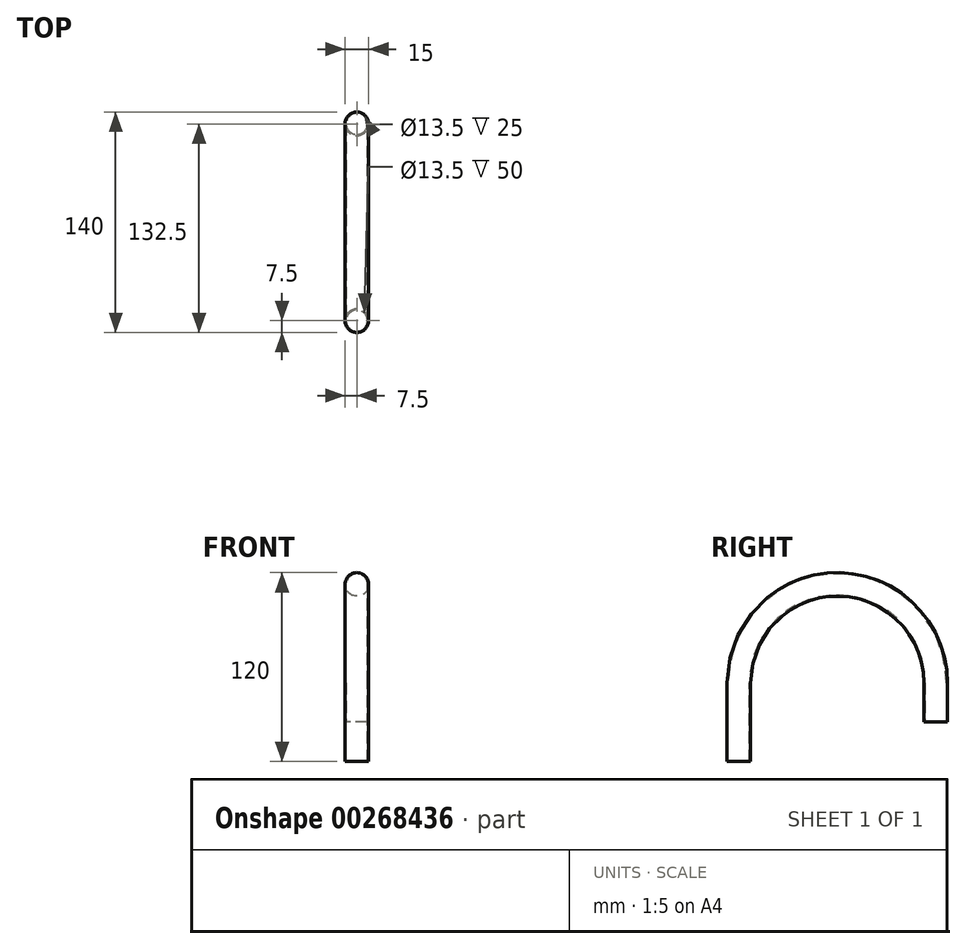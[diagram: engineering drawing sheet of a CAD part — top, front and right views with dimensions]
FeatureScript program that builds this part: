
annotation { "Feature Type Name" : "Feature", "Feature Type Description" : "" }
export const myFeature = defineFeature(function(context is Context, id is Id, definition is map)
    precondition{}
    {
        {
            var Q0;
            Q0=qCreatedBy(makeId("Top.planeOp"),FACE);
            var sketch = newSketch(context, id + "F0", { "sketchPlane" : qUnion([Q0])});
            skCircle(sketch, "E0", {"center": v(0, 0) * mm, "radius": 7.5 * mm});
            skCircle(sketch, "E1", {"center": v(0, 0) * mm, "radius": 6.75 * mm});
            skSolve(sketch);
        }
        {
            var Q0;
            Q0=qCreatedBy(makeId("Right.planeOp"),FACE);
            var sketch = newSketch(context, id + "F1", { "sketchPlane" : qUnion([Q0])});
            skLineSegment(sketch, "E2", {"start": v(0, 0) * mm, "end": v(0, 50) * mm});
            skArc(sketch, "E3", {"start": v(0, 50) * mm, "mid": v(62.5, 112.5) * mm, "end": v(125, 50) * mm});
            skLineSegment(sketch, "E4", {"start": v(125, 50) * mm, "end": v(125, 25) * mm});
            skSolve(sketch);
        }
        {
            var Q0;
            Q0=makeQuery(id+"F0.imprint","IMPRINT",FACE,{"disambiguationData":[TD([[makeQuery(id+"F0.imprint","IMPRINT",EDGE,{"derivedFrom":sQuery(id+"F0.wireOp",EDGE,"E0")}),1.0]])]});
            var Q1;
            Q1=sQuery(id+"F1.wireOp",EDGE,"E2");
            var Q2;
            Q2=sQuery(id+"F1.wireOp",EDGE,"E3");
            var Q3;
            Q3=sQuery(id+"F1.wireOp",EDGE,"E4");
            sweep(context, id + "F2", {"profiles" : qUnion([Q0]), "path" : qUnion([Q1, Q2, Q3])});
        }
    });
